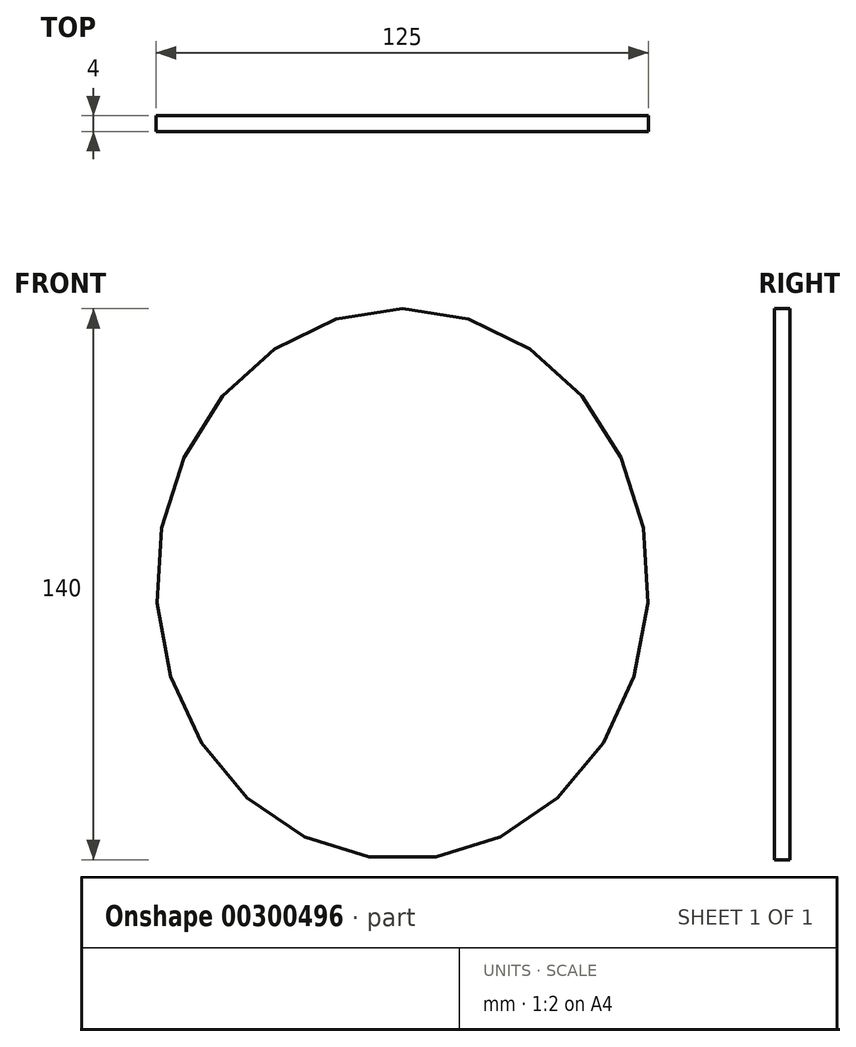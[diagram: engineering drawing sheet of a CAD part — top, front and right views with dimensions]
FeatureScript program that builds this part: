
annotation { "Feature Type Name" : "Feature", "Feature Type Description" : "" }
export const myFeature = defineFeature(function(context is Context, id is Id, definition is map)
    precondition{}
    {
        {
            var Q0;
            Q0=qCreatedBy(makeId("Front.planeOp"),FACE);
            var sketch = newSketch(context, id + "F0", { "sketchPlane" : qUnion([Q0])});
            skEllipse(sketch, "E0", {"center": v(0, 0) * mm, "majorRadius": 70 * mm, "minorRadius": 62.5 * mm, "majorAxis": v(0, 1)});
            skSolve(sketch);
        }
        {
            var Q0;
            Q0 = qSketchRegion(id + "F0", true);
            extrude(context, id + "F1", {"entities" : qUnion([Q0]), "depth" : 4 * mm});
        }
    });
